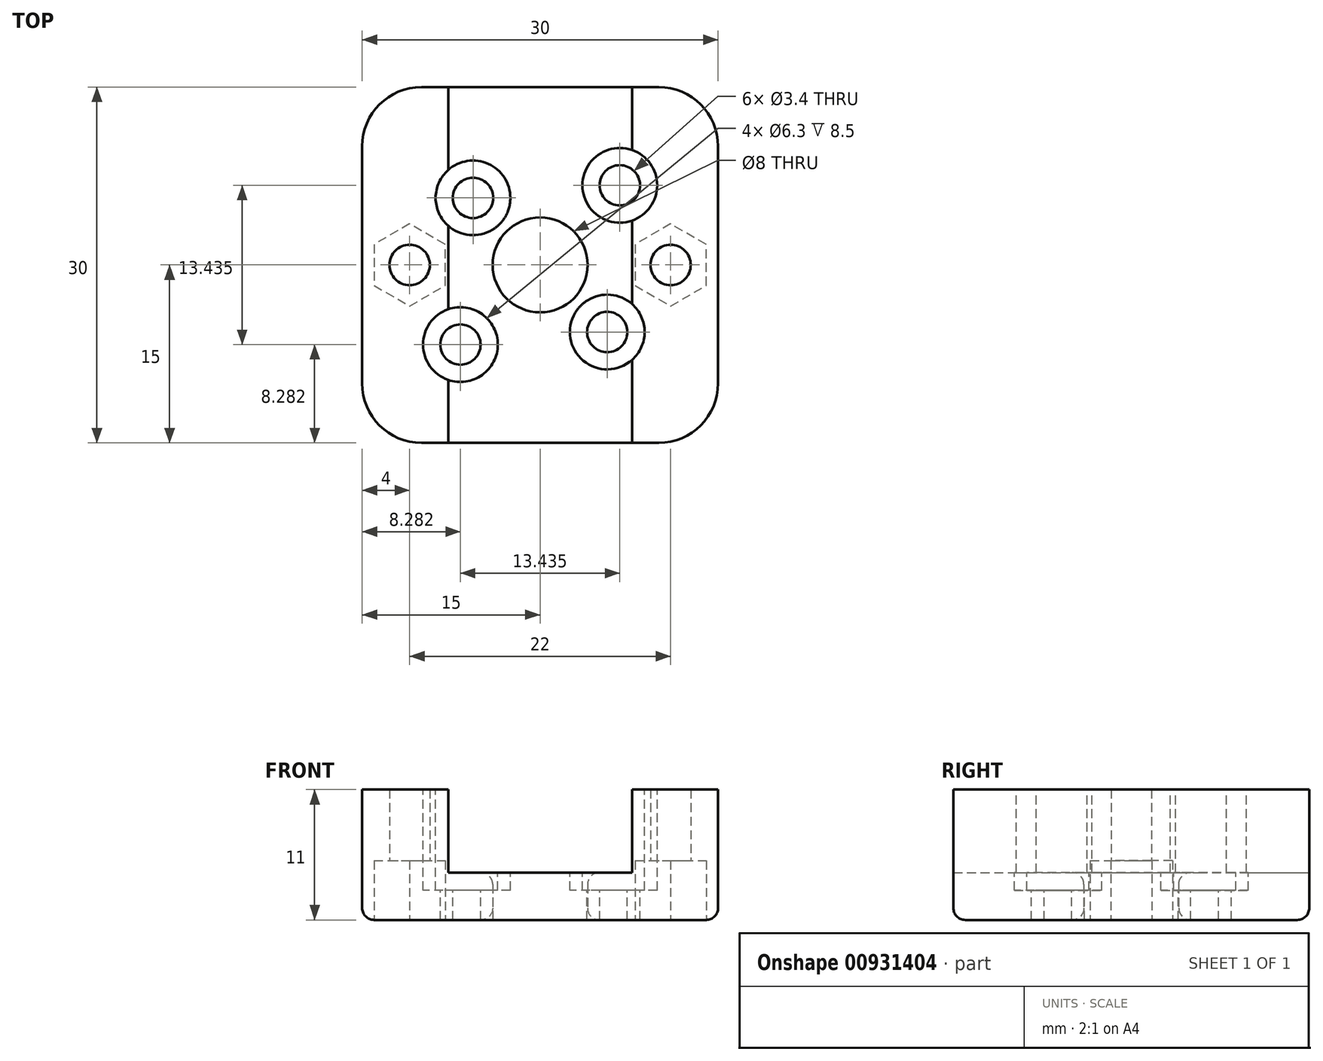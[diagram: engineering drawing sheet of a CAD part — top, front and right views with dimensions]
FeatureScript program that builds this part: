
annotation { "Feature Type Name" : "Feature", "Feature Type Description" : "" }
export const myFeature = defineFeature(function(context is Context, id is Id, definition is map)
    precondition{}
    {
        {
            var Q0;
            Q0=qCreatedBy(makeId("Top.planeOp"),FACE);
            var sketch = newSketch(context, id + "F0", { "sketchPlane" : qUnion([Q0])});
            skLineSegment(sketch, "E0.bottom", {"start": v(15, -15) * mm, "end": v(-15, -15) * mm});
            skLineSegment(sketch, "E0.top", {"start": v(15, 15) * mm, "end": v(-15, 15) * mm});
            skLineSegment(sketch, "E0.left", {"start": v(15, -15) * mm, "end": v(15, 15) * mm});
            skLineSegment(sketch, "E0.right", {"start": v(-15, -15) * mm, "end": v(-15, 15) * mm});
            skPoint(sketch, "E0.middle", {"position": v(0, 0) * mm});
            skCircle(sketch, "E1", {"center": v(0, 0) * mm, "radius": 4 * mm});
            skSolve(sketch);
        }
        {
            var Q0;
            Q0=makeQuery(id+"F0.imprint","IMPRINT",FACE,{"disambiguationData":[TD([[makeQuery(id+"F0.imprint","IMPRINT",EDGE,{"derivedFrom":sQuery(id+"F0.wireOp",EDGE,"E0.bottom")}),-1.0]])]});
            extrude(context, id + "F1", {"entities" : qUnion([Q0]), "depth" : 11 * mm, "offsetDistance" : 25 * mm});
        }
        {
            var Q0;
            Q0=makeQuery(id+"F1.opExtrude","CAP_FACE",FACE,{"disambiguationData":[OSD([sQuery(id+"F0.wireOp",EDGE,"E0.bottom"),sQuery(id+"F0.wireOp",EDGE,"E0.top"),sQuery(id+"F0.wireOp",EDGE,"E0.left"),sQuery(id+"F0.wireOp",EDGE,"E0.right"),sQuery(id+"F0.wireOp",EDGE,"E1")])],"isStart":false});
            var sketch = newSketch(context, id + "F2", { "sketchPlane" : qUnion([Q0])});
            skPoint(sketch, "E2", {"position": v(-6.72, -6.72) * mm});
            skPoint(sketch, "E3", {"position": v(-5.66, 5.66) * mm});
            skPoint(sketch, "E4", {"position": v(6.72, 6.72) * mm});
            skPoint(sketch, "E5", {"position": v(5.66, -5.66) * mm});
            skLineSegment(sketch, "E6", {"start": v(0, 0) * mm, "end": v(9.85, 9.85) * mm, "construction": true});
            skLineSegment(sketch, "E7", {"start": v(0, 0) * mm, "end": v(9.08, -9.08) * mm, "construction": true});
            skSolve(sketch);
        }
        {
            var Q0;
            Q0=sQuery(id+"F2.wireOp",VERTEX,"E2");
            var Q1;
            Q1=sQuery(id+"F2.wireOp",VERTEX,"E3");
            var Q2;
            Q2=sQuery(id+"F2.wireOp",VERTEX,"E4");
            var Q3;
            Q3=sQuery(id+"F2.wireOp",VERTEX,"E5");
            var Q4;
            Q4=makeQuery(id+"F1.opExtrude","SWEPT_BODY",BODY,{"disambiguationData":[OSD([sQuery(id+"F0.wireOp",EDGE,"E0.bottom"),sQuery(id+"F0.wireOp",EDGE,"E0.top"),sQuery(id+"F0.wireOp",EDGE,"E0.left"),sQuery(id+"F0.wireOp",EDGE,"E0.right"),sQuery(id+"F0.wireOp",EDGE,"E1")])]});
            hole(context, id + "F3", {"style" : HoleStyle.C_BORE, "endStyle" : HoleEndStyle.THROUGH, "holeDiameter" : 3.4 * mm, "cBoreDiameter" : 6.3 * mm, "cBoreDepth" : 8.5 * mm, "majorDiameter" : 5 * mm, "isTappedThrough" : true, "tappedDepth" : 12 * mm, "tapClearance" : 3, "locations" : qUnion([Q0, Q1, Q2, Q3]), "scope" : qUnion([Q4])});
        }
        {
            var Q0;
            Q0=makeQuery(id+"F1.opExtrude","CAP_FACE",FACE,{"disambiguationData":[OSD([sQuery(id+"F0.wireOp",EDGE,"E0.bottom"),sQuery(id+"F0.wireOp",EDGE,"E0.top"),sQuery(id+"F0.wireOp",EDGE,"E0.left"),sQuery(id+"F0.wireOp",EDGE,"E0.right"),sQuery(id+"F0.wireOp",EDGE,"E1")])],"isStart":true});
            var sketch = newSketch(context, id + "F4", { "sketchPlane" : qUnion([Q0])});
            skPoint(sketch, "E8", {"position": v(-11, 0) * mm});
            skPoint(sketch, "E9", {"position": v(11, 0) * mm});
            skCircle(sketch, "E10.cCircle", {"center": v(11, 0) * mm, "radius": 3 * mm, "construction": true});
            skLineSegment(sketch, "E10.0", {"start": v(14, 1.73) * mm, "end": v(14, -1.73) * mm});
            skLineSegment(sketch, "E10.1", {"start": v(14, -1.73) * mm, "end": v(11, -3.46) * mm});
            skLineSegment(sketch, "E10.2", {"start": v(11, -3.46) * mm, "end": v(8, -1.73) * mm});
            skLineSegment(sketch, "E10.3", {"start": v(8, -1.73) * mm, "end": v(8, 1.73) * mm});
            skLineSegment(sketch, "E10.4", {"start": v(8, 1.73) * mm, "end": v(11, 3.46) * mm});
            skLineSegment(sketch, "E10.5", {"start": v(11, 3.46) * mm, "end": v(14, 1.73) * mm});
            skPoint(sketch, "E10.0.midPoint", {"position": v(14, 0) * mm});
            skCircle(sketch, "E11.cCircle", {"center": v(-11, 0) * mm, "radius": 3 * mm, "construction": true});
            skLineSegment(sketch, "E11.0", {"start": v(-8, 1.73) * mm, "end": v(-8, -1.73) * mm});
            skLineSegment(sketch, "E11.1", {"start": v(-8, -1.73) * mm, "end": v(-11, -3.46) * mm});
            skLineSegment(sketch, "E11.2", {"start": v(-11, -3.46) * mm, "end": v(-14, -1.73) * mm});
            skLineSegment(sketch, "E11.3", {"start": v(-14, -1.73) * mm, "end": v(-14, 1.73) * mm});
            skLineSegment(sketch, "E11.4", {"start": v(-14, 1.73) * mm, "end": v(-11, 3.46) * mm});
            skLineSegment(sketch, "E11.5", {"start": v(-11, 3.46) * mm, "end": v(-8, 1.73) * mm});
            skPoint(sketch, "E11.0.midPoint", {"position": v(-8, 0) * mm});
            skSolve(sketch);
        }
        {
            var Q0;
            Q0=sQuery(id+"F4.wireOp",VERTEX,"E8");
            var Q1;
            Q1=sQuery(id+"F4.wireOp",VERTEX,"E9");
            var Q2;
            Q2=makeQuery(id+"F1.opExtrude","SWEPT_BODY",BODY,{"disambiguationData":[OSD([sQuery(id+"F0.wireOp",EDGE,"E0.bottom"),sQuery(id+"F0.wireOp",EDGE,"E0.top"),sQuery(id+"F0.wireOp",EDGE,"E0.left"),sQuery(id+"F0.wireOp",EDGE,"E0.right"),sQuery(id+"F0.wireOp",EDGE,"E1")])]});
            hole(context, id + "F5", {"style" : HoleStyle.SIMPLE, "endStyle" : HoleEndStyle.THROUGH, "standardTappedOrClearance" : lookupTablePath({ "fit" : "Normal", "standard" : "ISO", "size" : "M3", "type" : "Clearance" }), "standardBlindInLast" : lookupTablePath({ "fit" : "Normal", "standard" : "ISO", "engagement" : "75%", "pitch" : "0.5 mm", "size" : "M3", "type" : "Clearance & tapped" }), "holeDiameter" : 3.4 * mm, "majorDiameter" : 5 * mm, "isTappedThrough" : true, "tappedDepth" : 12 * mm, "tapClearance" : 3, "locations" : qUnion([Q0, Q1]), "scope" : qUnion([Q2])});
        }
        {
            var Q0;
            Q0 = qSketchRegion(id + "F4", true);
            extrude(context, id + "F6", {"entities" : qUnion([Q0]), "operationType" : NewBodyOperationType.REMOVE, "oppositeDirection" : true, "depth" : 5 * mm, "offsetDistance" : 25 * mm});
        }
        {
            var Q0;
            Q0=makeQuery(id+"F1.opExtrude","CAP_FACE",FACE,{"disambiguationData":[OSD([sQuery(id+"F0.wireOp",EDGE,"E0.bottom"),sQuery(id+"F0.wireOp",EDGE,"E0.top"),sQuery(id+"F0.wireOp",EDGE,"E0.left"),sQuery(id+"F0.wireOp",EDGE,"E0.right"),sQuery(id+"F0.wireOp",EDGE,"E1")])],"isStart":false});
            var sketch = newSketch(context, id + "F7", { "sketchPlane" : qUnion([Q0])});
            skLineSegment(sketch, "E12.bottom", {"start": v(7.75, -15) * mm, "end": v(-7.75, -15) * mm});
            skLineSegment(sketch, "E12.top", {"start": v(7.75, 15) * mm, "end": v(-7.75, 15) * mm});
            skLineSegment(sketch, "E12.left", {"start": v(7.75, -15) * mm, "end": v(7.75, 15) * mm});
            skLineSegment(sketch, "E12.right", {"start": v(-7.75, -15) * mm, "end": v(-7.75, 15) * mm});
            skPoint(sketch, "E12.middle", {"position": v(0, 0) * mm});
            skSolve(sketch);
        }
        {
            var Q0;
            {var subQ5=sQuery(id+"F7.wireOp",EDGE,"E12.bottom");Q0=makeQuery(id+"F7.imprint","IMPRINT",FACE,{"disambiguationData":[TD([[makeQuery(id+"F7.imprint","IMPRINT",EDGE,{"derivedFrom":subQ5}),-1.0]])]});}
            extrude(context, id + "F8", {"entities" : qUnion([Q0]), "operationType" : NewBodyOperationType.REMOVE, "oppositeDirection" : true, "depth" : 7 * mm, "offsetDistance" : 25 * mm});
        }
        {
            var Q0;
            Q0=makeQuery(id+"F1.opExtrude","SWEPT_EDGE",EDGE,{"disambiguationData":[OSD([sQuery(id+"F0.wireOp",EDGE,"E0.top"),sQuery(id+"F0.wireOp",EDGE,"E0.left")])]});
            var Q1;
            Q1=makeQuery(id+"F1.opExtrude","SWEPT_EDGE",EDGE,{"disambiguationData":[OSD([sQuery(id+"F0.wireOp",EDGE,"E0.top"),sQuery(id+"F0.wireOp",EDGE,"E0.right")])]});
            var Q2;
            Q2=makeQuery(id+"F1.opExtrude","SWEPT_EDGE",EDGE,{"disambiguationData":[OSD([sQuery(id+"F0.wireOp",EDGE,"E0.bottom"),sQuery(id+"F0.wireOp",EDGE,"E0.left")])]});
            var Q3;
            Q3=makeQuery(id+"F1.opExtrude","SWEPT_EDGE",EDGE,{"disambiguationData":[OSD([sQuery(id+"F0.wireOp",EDGE,"E0.bottom"),sQuery(id+"F0.wireOp",EDGE,"E0.right")])]});
            fillet(context, id + "F9", {"entities" : qUnion([Q0, Q1, Q2, Q3]), "radius" : 5 * mm, "tangentPropagation" : true, "allowEdgeOverflow" : false});
        }
        {
            var Q0;
            Q0=makeQuery(id+"F8.boolean.opBoolean","COPY",EDGE,{"derivedFrom":makeQuery(id+"F8.opExtrude","CAP_EDGE",EDGE,{"disambiguationData":[OSD([sQuery(id+"F0.wireOp",EDGE,"E1")])],"isStart":false})});
            var Q1;
            Q1=makeQuery(id+"F1.opExtrude","SWEPT_FACE",FACE,{"disambiguationData":[OSD([sQuery(id+"F0.wireOp",EDGE,"E1")])]});
            var Q2;
            {var subQ0=sQuery(id+"F0.wireOp",EDGE,"E0.right");var subQ1=sQuery(id+"F0.wireOp",EDGE,"E0.bottom");Q2=makeQuery(id+"F9.opFillet","BLEND_EDGE",EDGE,{"blendedFrom":[makeQuery(id+"F1.opExtrude","SWEPT_EDGE",EDGE,{"disambiguationData":[OSD([subQ1,subQ0])]}),makeQuery(id+"F1.opExtrude","CAP_FACE",FACE,{"disambiguationData":[OSD([subQ1,sQuery(id+"F0.wireOp",EDGE,"E0.top"),sQuery(id+"F0.wireOp",EDGE,"E0.left"),subQ0,sQuery(id+"F0.wireOp",EDGE,"E1")])],"isStart":true})],"blendedInto":[makeQuery(id+"F1.opExtrude","CAP_FACE",FACE,{"disambiguationData":[OSD([subQ1,sQuery(id+"F0.wireOp",EDGE,"E0.top"),sQuery(id+"F0.wireOp",EDGE,"E0.left"),subQ0,sQuery(id+"F0.wireOp",EDGE,"E1")])],"isStart":true})]});}
            var Q3;
            Q3=makeQuery(id+"F8.boolean.opBoolean","COPY",EDGE,{"derivedFrom":makeQuery(id+"F8.opExtrude","SWEPT_EDGE",EDGE,{"disambiguationData":[OSD([sQuery(id+"F0.wireOp",EDGE,"E0.top"),sQuery(id+"F7.wireOp",EDGE,"E12.top"),sQuery(id+"F7.wireOp",EDGE,"E12.left")])]})});
            var Q4;
            Q4=makeQuery(id+"F8.boolean.opBoolean","COPY",EDGE,{"derivedFrom":makeQuery(id+"F8.opExtrude","SWEPT_EDGE",EDGE,{"disambiguationData":[OSD([sQuery(id+"F0.wireOp",EDGE,"E0.top"),sQuery(id+"F7.wireOp",EDGE,"E12.top"),sQuery(id+"F7.wireOp",EDGE,"E12.right")])]})});
            var Q5;
            Q5=makeQuery(id+"F8.boolean.opBoolean","COPY",EDGE,{"derivedFrom":makeQuery(id+"F8.opExtrude","SWEPT_EDGE",EDGE,{"disambiguationData":[OSD([sQuery(id+"F0.wireOp",EDGE,"E0.bottom"),sQuery(id+"F7.wireOp",EDGE,"E12.bottom"),sQuery(id+"F7.wireOp",EDGE,"E12.left")])]})});
            var Q6;
            Q6=makeQuery(id+"F8.boolean.opBoolean","COPY",EDGE,{"derivedFrom":makeQuery(id+"F8.opExtrude","SWEPT_EDGE",EDGE,{"disambiguationData":[OSD([sQuery(id+"F0.wireOp",EDGE,"E0.bottom"),sQuery(id+"F7.wireOp",EDGE,"E12.bottom"),sQuery(id+"F7.wireOp",EDGE,"E12.right")])]})});
            fillet(context, id + "F10", {"entities" : qUnion([Q0, Q1, Q2, Q3, Q4, Q5, Q6]), "radius" : 1 * mm, "tangentPropagation" : true, "allowEdgeOverflow" : false});
        }
    });
